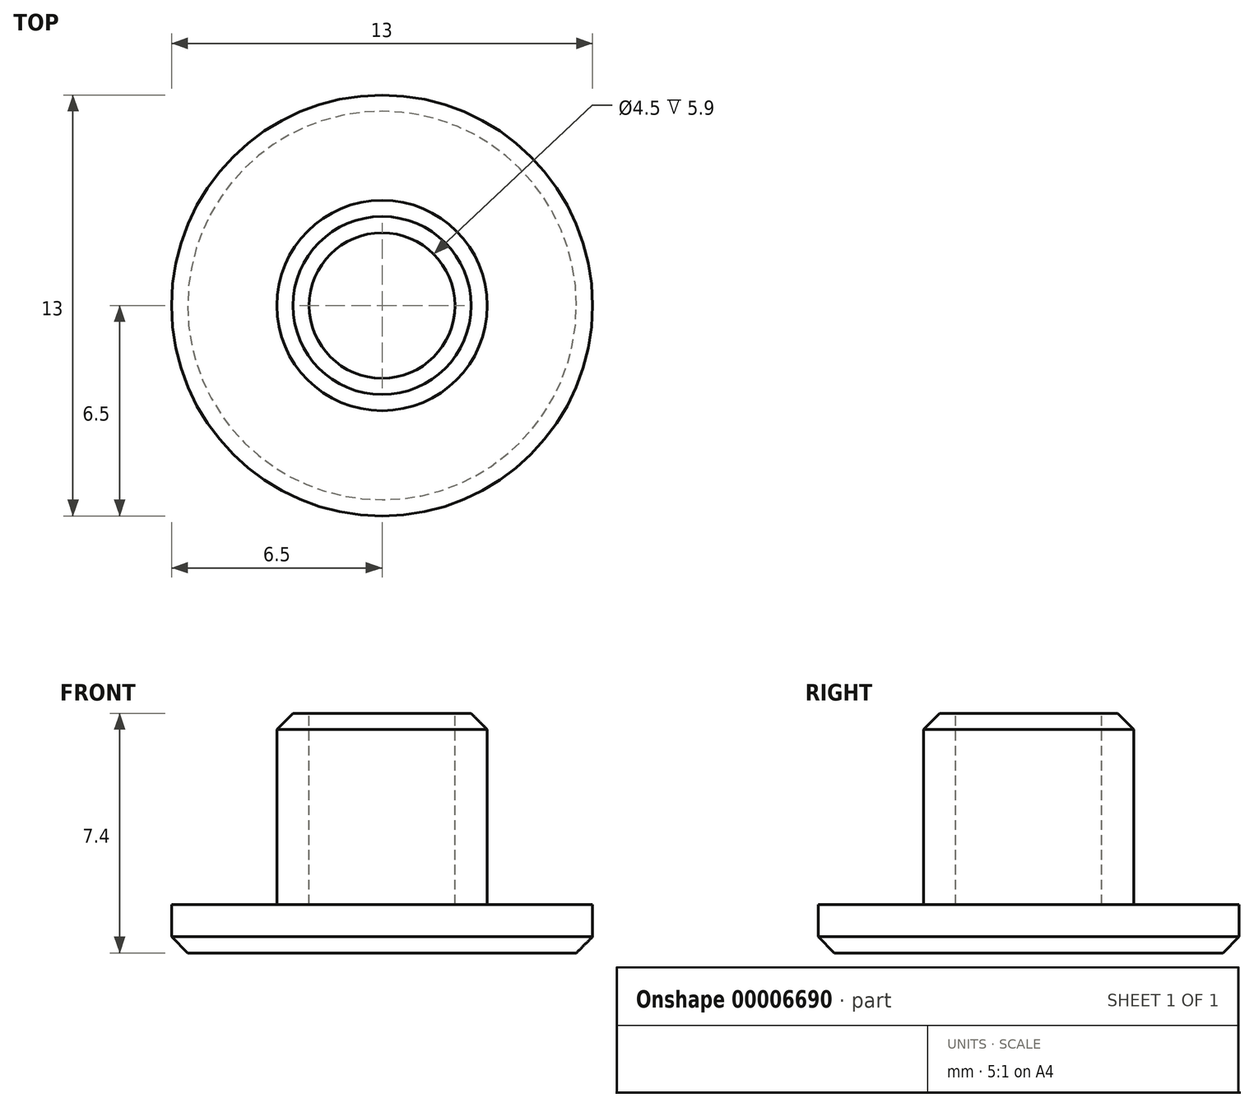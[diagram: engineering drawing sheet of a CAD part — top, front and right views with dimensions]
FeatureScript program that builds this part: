
annotation { "Feature Type Name" : "Feature", "Feature Type Description" : "" }
export const myFeature = defineFeature(function(context is Context, id is Id, definition is map)
    precondition{}
    {
        {
            var Q0;
            Q0=qCreatedBy(makeId("Top.planeOp"),FACE);
            var sketch = newSketch(context, id + "F0", { "sketchPlane" : qUnion([Q0])});
            skCircle(sketch, "E0", {"center": v(0, 0) * mm, "radius": 6.5 * mm});
            skSolve(sketch);
        }
        {
            var Q0;
            Q0=makeQuery(id+"F0.imprint","IMPRINT",FACE,{"disambiguationData":[TD([[makeQuery(id+"F0.imprint","IMPRINT",EDGE,{"derivedFrom":sQuery(id+"F0.wireOp",EDGE,"E0")}),1.0]])]});
            extrude(context, id + "F1", {"entities" : qUnion([Q0]), "depth" : 1.5 * mm});
        }
        {
            var Q0;
            Q0=makeQuery(id+"F1.opExtrude","CAP_FACE",FACE,{"disambiguationData":[OSD([sQuery(id+"F0.wireOp",EDGE,"E0")])],"isStart":false});
            var sketch = newSketch(context, id + "F2", { "sketchPlane" : qUnion([Q0])});
            skCircle(sketch, "E1", {"center": v(0, 0) * mm, "radius": 3.25 * mm});
            skSolve(sketch);
        }
        {
            var Q0;
            Q0 = qSketchRegion(id + "F2", true);
            extrude(context, id + "F3", {"entities" : qUnion([Q0]), "operationType" : NewBodyOperationType.ADD, "depth" : 5.9 * mm});
        }
        {
            var Q0;
            Q0=makeQuery(id+"F3.opExtrude","CAP_FACE",FACE,{"disambiguationData":[OSD([sQuery(id+"F2.wireOp",EDGE,"E1")])],"isStart":false});
            var sketch = newSketch(context, id + "F4", { "sketchPlane" : qUnion([Q0])});
            skCircle(sketch, "E2", {"center": v(0, 0) * mm, "radius": 2.25 * mm});
            skSolve(sketch);
        }
        {
            var Q0;
            Q0 = qSketchRegion(id + "F4", true);
            var Q1;
            Q1=makeQuery(id+"F1.opExtrude","CAP_FACE",FACE,{"disambiguationData":[OSD([sQuery(id+"F0.wireOp",EDGE,"E0")])],"isStart":false});
            extrude(context, id + "F5", {"entities" : qUnion([Q0]), "operationType" : NewBodyOperationType.REMOVE, "endBound" : BoundingType.UP_TO_SURFACE, "oppositeDirection" : true, "endBoundEntityFace" : qUnion([Q1]), "depth" : 25 * mm});
        }
        {
            var Q0;
            Q0=makeQuery(id+"F3.opExtrude","CAP_EDGE",EDGE,{"disambiguationData":[OSD([sQuery(id+"F2.wireOp",EDGE,"E1")])],"isStart":false});
            chamfer(context, id + "F6", {"entities" : qUnion([Q0]), "width" : .5 * mm, "tangentPropagation" : true});
        }
        {
            var Q0;
            Q0=makeQuery(id+"F1.opExtrude","CAP_EDGE",EDGE,{"disambiguationData":[OSD([sQuery(id+"F0.wireOp",EDGE,"E0")])],"isStart":true});
            chamfer(context, id + "F7", {"entities" : qUnion([Q0]), "width" : .5 * mm, "tangentPropagation" : true});
        }
    });
